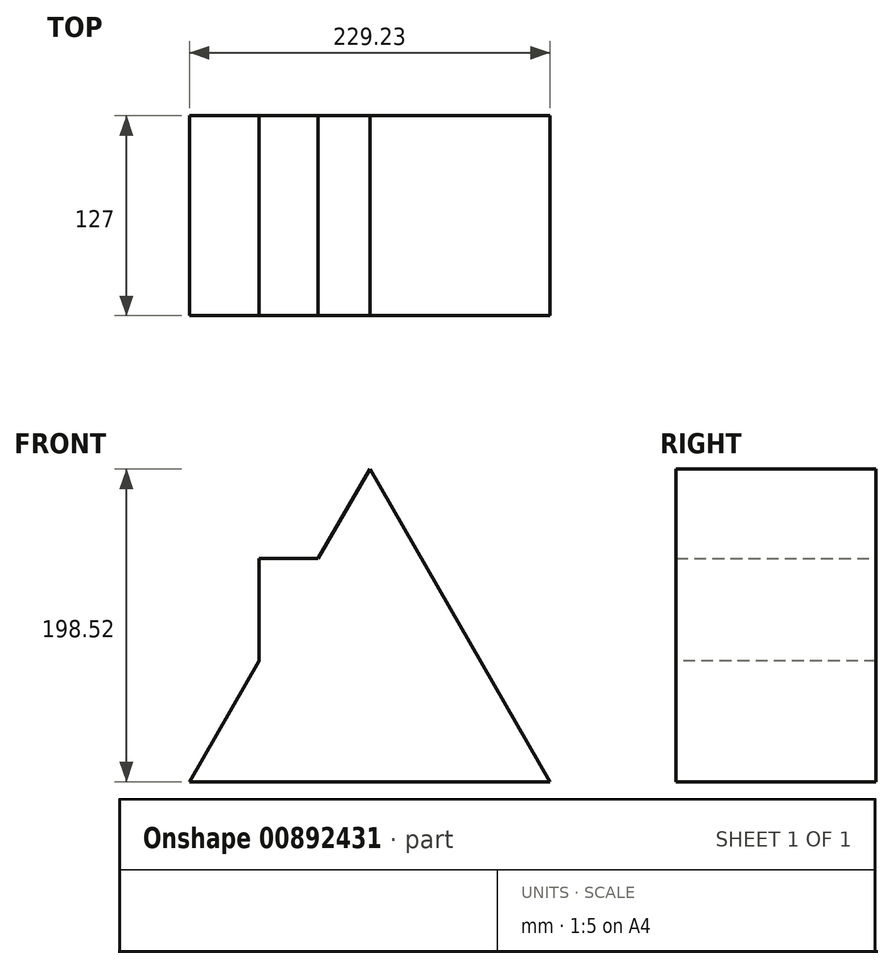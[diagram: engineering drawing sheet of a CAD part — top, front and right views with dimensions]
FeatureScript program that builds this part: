
annotation { "Feature Type Name" : "Feature", "Feature Type Description" : "" }
export const myFeature = defineFeature(function(context is Context, id is Id, definition is map)
    precondition{}
    {
        {
            var Q0;
            Q0=qCreatedBy(makeId("Front.planeOp"),FACE);
            var sketch = newSketch(context, id + "F0", { "sketchPlane" : qUnion([Q0])});
            skLineSegment(sketch, "E0.bottom", {"start": v(54.85, 60.73) * mm, "end": v(-41.78, 60.73) * mm});
            skLineSegment(sketch, "E0.top", {"start": v(54.85, -40.68) * mm, "end": v(-41.78, -40.68) * mm});
            skLineSegment(sketch, "E0.left", {"start": v(54.85, 60.73) * mm, "end": v(54.85, -40.68) * mm});
            skLineSegment(sketch, "E0.right", {"start": v(-41.78, 60.73) * mm, "end": v(-41.78, -40.68) * mm});
            skSolve(sketch);
        }
        {
            var Q0;
            Q0=makeQuery(id+"F0.imprint","IMPRINT",FACE,{"disambiguationData":[TD([[makeQuery(id+"F0.imprint","IMPRINT",EDGE,{"derivedFrom":sQuery(id+"F0.wireOp",EDGE,"E0.bottom")}),1.0]])]});
            extrude(context, id + "F1", {"entities" : qUnion([Q0]), "depth" : 127 * mm, "offsetDistance" : 25.4 * mm});
        }
        {
            var Q0;
            Q0=qCreatedBy(makeId("Front.planeOp"),FACE);
            var sketch = newSketch(context, id + "F2", { "sketchPlane" : qUnion([Q0])});
            skCircle(sketch, "E1.cCircle", {"center": v(28.56, -14.8) * mm, "radius": 66.17 * mm, "construction": true});
            skLineSegment(sketch, "E1.0", {"start": v(143.17, -80.98) * mm, "end": v(-86.06, -80.98) * mm});
            skLineSegment(sketch, "E1.1", {"start": v(-86.06, -80.98) * mm, "end": v(28.56, 117.54) * mm});
            skLineSegment(sketch, "E1.2", {"start": v(28.56, 117.54) * mm, "end": v(143.17, -80.98) * mm});
            skPoint(sketch, "E1.0.midPoint", {"position": v(28.56, -80.98) * mm});
            skSolve(sketch);
        }
        {
            var Q0;
            Q0=makeQuery(id+"F2.imprint","IMPRINT",FACE,{"disambiguationData":[TD([[makeQuery(id+"F2.imprint","IMPRINT",EDGE,{"derivedFrom":sQuery(id+"F2.wireOp",EDGE,"E1.0")}),-1.0]])]});
            extrude(context, id + "F3", {"entities" : qUnion([Q0]), "operationType" : NewBodyOperationType.ADD, "depth" : 127 * mm, "offsetDistance" : 25.4 * mm});
        }
    });
